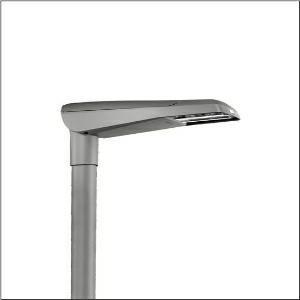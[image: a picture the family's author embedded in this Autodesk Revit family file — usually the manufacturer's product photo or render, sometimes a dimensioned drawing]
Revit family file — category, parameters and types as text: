
# Revit family: streetlight_sl_11_iq_micro___st1_0ab_5xc1n51f08ce_cbf6
name_source: partatom
category: Lighting Fixtures
units: mm (PartAtom-declared; Revit-internal decimal feet)

## family parameters
Cut with Voids When Loaded = No
Host = Face
Light Source = No
Part Type = Normal
Room Calculation Point = No
Round Connector Dimension = Use Diameter
Shared = No

## types (1)
- --- (1 x LED, 1580 lm, 12.6 W, 3000K)
    Apparent Load = 13 VA
    CIE Flux Codes = 29 63 95 100 100
    Color Rendering = 70
    Color Temperature = 3000K
    Default Elevation = 1800 mm
    Description = Streetlight SL 11 iQ micro, mast luminaire, primary light control with 3 zone facetted reflector, of plastic, silver coated, highly specular, primary optical cover: cover, of PMMA, transparent, light distribution: ST1.0aB, light emission: direct distribution, primary light characteristic: asymmetric, installation type: post-top, side-entry, lamps: LED, High Power LED, rated values: 1.580lm | 12,6W | 125,4lm/W (begin service life); end service life: 1.580lm | 12,9W; at 50% lumin. flux: 790lm | 6,8W | 116,2lm/W, colour temperature: 3000K, colour rendering: CRI > 70, light colour: 730, light setting 1 begin service life: 100% | 1.580lm | 12,6W | 125,4lm/W | 3.000K, light setting 1 end service life: 12,9W, further light settings possible, control: optimised constant luminous flux control (CLO 2.0), Desk-Remote (wireless, voltage-free reading and setting of iQ features in the workshop via application-optimized NFC function/RFID function), Light-Fading, Smart-Wire, Night-Set, Lumen-Switch, Temp-Guard, Auto-Match, Street-Remote, with cable H07RN-F 5x 1.5mm², mains connection: 230..240V, AC, 50/60Hz, connection cable pre-assembled, cable length: 5,5m, luminaire housing, of diecast aluminium, powder-coated, Siteco® metallic grey (DB 702S), please order mast flange separately, inclination adjustable without tools: 0°, 5°, 10°, 15° (post-top) | 0°, -5°, -10°, -15° (side-entry), sealing non-destructively replaceable, multi-level sealing system, length: 600mm, width: 174mm, height: 116mm, mast flange for spigot size: 42mm (side-entry): 5XC10008XM4, 60/48mm (side-entry/post-top): 5XC10108XM2, 76/60mm (side-entry/post-top): 5XC10108XM1, equipment: standard, protection rating (complete): IP66, insulation class (complete): insulation class II (safety insulation), certification: CE, ENEC, ENEC+, VDE, impact resistance: IK10, permissible operating ambient temperature for outdoor applications: -25..+50°C, standard-compliant lighting for roads and squares, Environmental Product Declaration (EPD) tested and certified by an independent institute, packaging unit: 1 piece

Light Distribution: ST1.0aB
    Height = 116 mm
    Lamp = 1 x LED
    Lamp Light Flux = 1580 lm
    Lamp Power = 12.6 W
    Lamp count = 1
    Length = 600 mm
    Luminous efficacy = 125 lm/W
    Manufacturer = Siteco
    ModVariant = No
    Model = 5XC1N51F08CE
    Number of Poles = 1
    OnlyDefault = Yes
    Power Factor = 1
    Product Name = Streetlight SL 11 iQ micro | ST1.0aB
    Product group = mast luminaire | pylon top
    ProductGroupID = 6100
    Protection Class = Protection class II
    Protection Degree = IP 66
    RLX_Detail_Level = 1
    RLX_Emergency_Light_Flux = 0 lm
    RLX_Emergency_Type = 0
    RLX_Emergency_Type_DB = No
    RlxData = <blob elided: 26245 chars, md5=f702f512>
    Socket = socket
    Standby Power = 0 W
    System Light Flux = 1580 lm
    System Power = 13 W
    Type Comments = factory setting: luminous flux: 100 % | dim-lin: 254 | 229 mA
    Type Image = l_1006566.jpg
    URL = http://relux.com
    VarID = @adj_019797
    Voltage = 0 V
    Weight = 0.00 kg
    Width = 174 mm

## geometry (parser evidence)
native form markers: Blend x4, Sweep x9
no freeform markers — native parametric forms only
